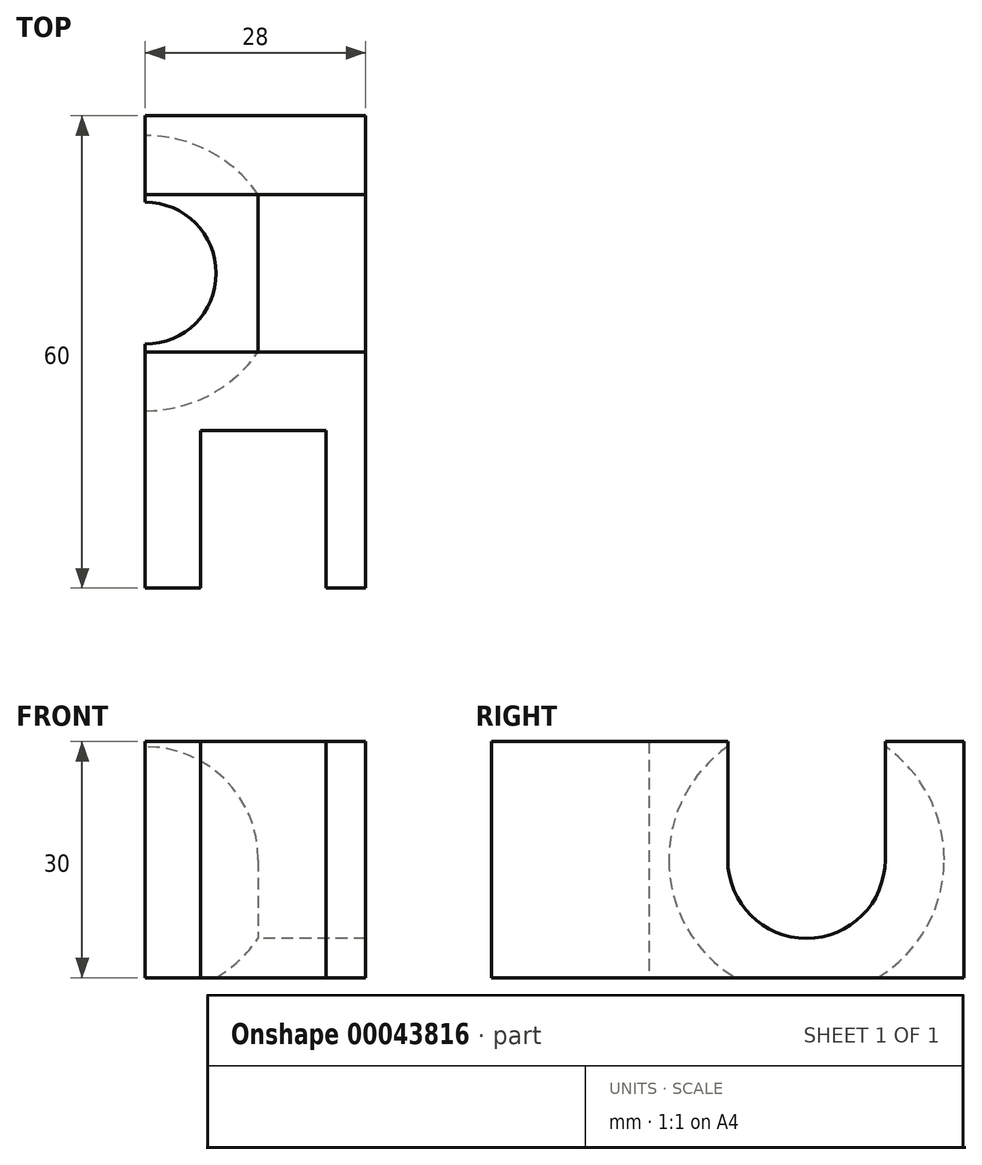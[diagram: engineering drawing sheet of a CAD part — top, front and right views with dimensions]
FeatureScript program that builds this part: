
annotation { "Feature Type Name" : "Feature", "Feature Type Description" : "" }
export const myFeature = defineFeature(function(context is Context, id is Id, definition is map)
    precondition{}
    {
        {
            var Q0;
            Q0=qCreatedBy(makeId("Top.planeOp"),FACE);
            var sketch = newSketch(context, id + "F0", { "sketchPlane" : qUnion([Q0])});
            skLineSegment(sketch, "E0", {"start": v(0, 0) * mm, "end": v(7, 0) * mm});
            skLineSegment(sketch, "E1", {"start": v(7, 0) * mm, "end": v(7, 20) * mm});
            skLineSegment(sketch, "E2", {"start": v(7, 20) * mm, "end": v(23, 20) * mm});
            skLineSegment(sketch, "E3", {"start": v(23, 20) * mm, "end": v(23, 0) * mm});
            skLineSegment(sketch, "E4", {"start": v(23, 0) * mm, "end": v(28, 0) * mm});
            skLineSegment(sketch, "E5", {"start": v(28, 0) * mm, "end": v(28, 60) * mm});
            skLineSegment(sketch, "E6", {"start": v(28, 60) * mm, "end": v(0, 60) * mm});
            skLineSegment(sketch, "E7", {"start": v(0, 60) * mm, "end": v(0, -1.84) * mm});
            skSolve(sketch);
        }
        {
            var Q0;
            Q0=qSketchRegion(id+"F0",true);
            extrude(context, id + "F1", {"entities" : qUnion([Q0]), "depth" : 30 * mm});
        }
        {
            var Q0;
            Q0=makeQuery(id+"F1.opExtrude","SWEPT_FACE",FACE,{"disambiguationData":[OSD([sQuery(id+"F0.wireOp",EDGE,"E7")])]});
            var sketch = newSketch(context, id + "F2", { "sketchPlane" : qUnion([Q0])});
            skLineSegment(sketch, "E8.0", {"start": v(-20, 30) * mm, "end": v(-20, 0) * mm});
            skLineSegment(sketch, "E9", {"start": v(-20, 30) * mm, "end": v(-60, 0) * mm, "construction": true});
            skCircle(sketch, "E10", {"center": v(-40, 15) * mm, "radius": 10 * mm});
            skLineSegment(sketch, "E11", {"start": v(-50, 15) * mm, "end": v(-50, 30) * mm});
            skLineSegment(sketch, "E12", {"start": v(-30, 15) * mm, "end": v(-30, 30) * mm});
            skLineSegment(sketch, "E13", {"start": v(-60, 15) * mm, "end": v(-20, 15) * mm, "construction": true});
            skArc(sketch, "E14", {"start": v(-57.5, 15) * mm, "mid": v(-40, -2.5) * mm, "end": v(-22.5, 15) * mm});
            skLineSegment(sketch, "E15", {"start": v(-57.5, 15) * mm, "end": v(-22.5, 15) * mm});
            skSolve(sketch);
        }
        {
            var Q0;
            {var subQ0=sQuery(id+"F2.wireOp",EDGE,"E15");var subQ1=sQuery(id+"F2.wireOp",EDGE,"E10");var subQ3=makeQuery(id+"F2.imprint","INTERSECT",VERTEX,{"derivedFrom":[subQ1,sQuery(id+"F2.wireOp",EDGE,"E11"),subQ0]});Q0=makeQuery(id+"F2.imprint","IMPRINT",FACE,{"disambiguationData":[TD([[makeQuery(id+"F2.imprint","IMPRINT",EDGE,{"disambiguationData":[TD([[subQ3,-1.0]])],"derivedFrom":subQ1}),1.0]])]});}
            var Q1;
            {var subQ0=sQuery(id+"F2.wireOp",EDGE,"E15");var subQ1=sQuery(id+"F2.wireOp",EDGE,"E10");var subQ3=makeQuery(id+"F2.imprint","INTERSECT",VERTEX,{"derivedFrom":[subQ1,sQuery(id+"F2.wireOp",EDGE,"E11"),subQ0]});Q1=makeQuery(id+"F2.imprint","IMPRINT",FACE,{"disambiguationData":[TD([[makeQuery(id+"F2.imprint","IMPRINT",EDGE,{"disambiguationData":[TD([[subQ3,1.0]])],"derivedFrom":subQ1}),1.0]])]});}
            var Q2;
            {var subQ2=sQuery(id+"F2.wireOp",EDGE,"E11");Q2=makeQuery(id+"F2.imprint","IMPRINT",FACE,{"disambiguationData":[TD([[makeQuery(id+"F2.imprint","IMPRINT",EDGE,{"derivedFrom":subQ2}),-1.0]])]});}
            extrude(context, id + "F3", {"entities" : qUnion([Q0, Q1, Q2]), "operationType" : NewBodyOperationType.REMOVE, "endBound" : BoundingType.UP_TO_NEXT, "oppositeDirection" : true, "depth" : 25 * mm});
        }
        {
            var Q0;
            {var subQ0=sQuery(id+"F2.wireOp",EDGE,"E15");var subQ1=sQuery(id+"F2.wireOp",EDGE,"E10");var subQ3=makeQuery(id+"F2.imprint","INTERSECT",VERTEX,{"derivedFrom":[subQ1,sQuery(id+"F2.wireOp",EDGE,"E11"),subQ0]});Q0=makeQuery(id+"F2.imprint","IMPRINT",FACE,{"disambiguationData":[TD([[makeQuery(id+"F2.imprint","IMPRINT",EDGE,{"disambiguationData":[TD([[subQ3,-1.0]])],"derivedFrom":subQ1}),1.0]])]});}
            var Q1;
            {var subQ1=sQuery(id+"F2.wireOp",EDGE,"E14");var subQ4=sQuery(id+"F2.wireOp",EDGE,"E15");var subQ9=makeQuery(id+"F2.imprint","INTERSECT",VERTEX,{"disambiguationData":[OD(0.0)],"derivedFrom":[subQ1,subQ4]});Q1=makeQuery(id+"F2.imprint","IMPRINT",FACE,{"disambiguationData":[TD([[makeQuery(id+"F2.imprint","IMPRINT",EDGE,{"disambiguationData":[TD([[subQ9,-1.0]])],"derivedFrom":subQ1}),1.0]])]});}
            var Q2;
            {var subQ0=makeQuery(id+"F1.opExtrude","CAP_EDGE",EDGE,{"disambiguationData":[OSD([sQuery(id+"F0.wireOp",EDGE,"E7")])],"isStart":true});var subQ1=sQuery(id+"F2.wireOp",EDGE,"E14");var subQ3=makeQuery(id+"F2.imprint","INTERSECT",VERTEX,{"disambiguationData":[OD(0.0)],"derivedFrom":[subQ0,subQ1]});Q2=makeQuery(id+"F2.imprint","IMPRINT",FACE,{"disambiguationData":[TD([[makeQuery(id+"F2.imprint","IMPRINT",EDGE,{"disambiguationData":[TD([[subQ3,-1.0]])],"derivedFrom":subQ1}),1.0]])]});}
            var Q3;
            Q3=sQuery(id+"F2.wireOp",EDGE,"E15");
            revolve(context, id + "F4", {"operationType" : NewBodyOperationType.REMOVE, "entities" : qUnion([Q0, Q1, Q2]), "axis" : qUnion([Q3]), "revolveType" : RevolveType.FULL, "oppositeDirection" : true});
        }
    });
